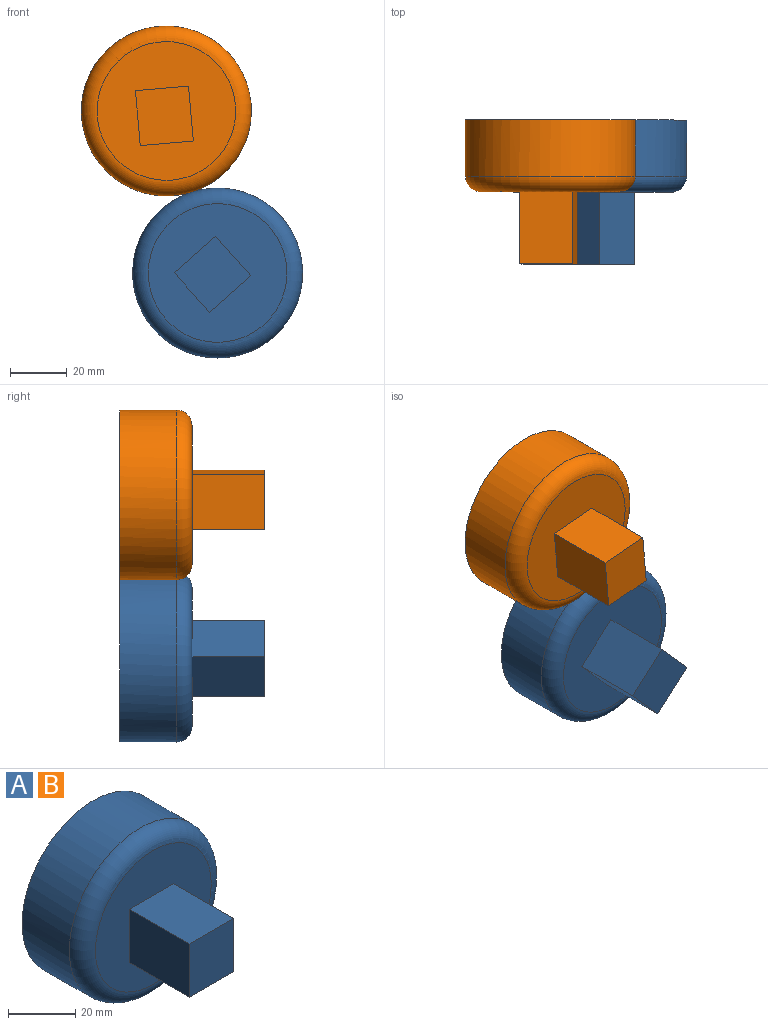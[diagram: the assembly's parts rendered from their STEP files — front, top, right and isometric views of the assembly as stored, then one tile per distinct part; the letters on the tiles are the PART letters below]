
ASSEMBLY  parts=2 mates=1
PART A: 9 faces, bbox 64.8x50.8x64.8 mm
  f0: plane 48.83x48.83mm, normal (0,-1,0), area 1508.9mm2, adj f3,f4,f5,f6,f7
  f1: cylinder r=29.94mm len=59.87mm, axis (0,1,0), area 3739.5mm2, adj f2,f3
  f2: plane 59.87x59.87mm, normal (0,1,0), area 2815.4mm2, adj f1
  f3: torus R=24.42mm, axis (0,-1,0), area 1521.4mm2, adj f0,f1
  f4: plane 25.4x19.42mm, normal (-1,0,0), area 493.2mm2, adj f0,f5,f7,f8
  f5: plane 25.4x18.75mm, normal (0,0,-1), area 476.3mm2, adj f0,f4,f6,f8
  f6: plane 25.4x19.42mm, normal (1,0,0), area 493.2mm2, adj f0,f5,f7,f8
  f7: plane 25.4x18.75mm, normal (0,0,1), area 476.3mm2, adj f0,f4,f6,f8
  f8: plane 19.42x18.75mm, normal (0,-1,0), area 364.1mm2, adj f4,f5,f6,f7
PART B: same geometry as A
PLACE A rot(axis=(0,1,0),48.4deg) t=(-43.84,-9.35,-115.06)mm
PLACE B rot(axis=(0,-1,0),5deg) t=(-8.86,-9.35,-19.66)mm fixed
MATE planar B.f1 <-> A.f1  axis (0,1,0) through (-73.52,-9.35,13.98)mm
